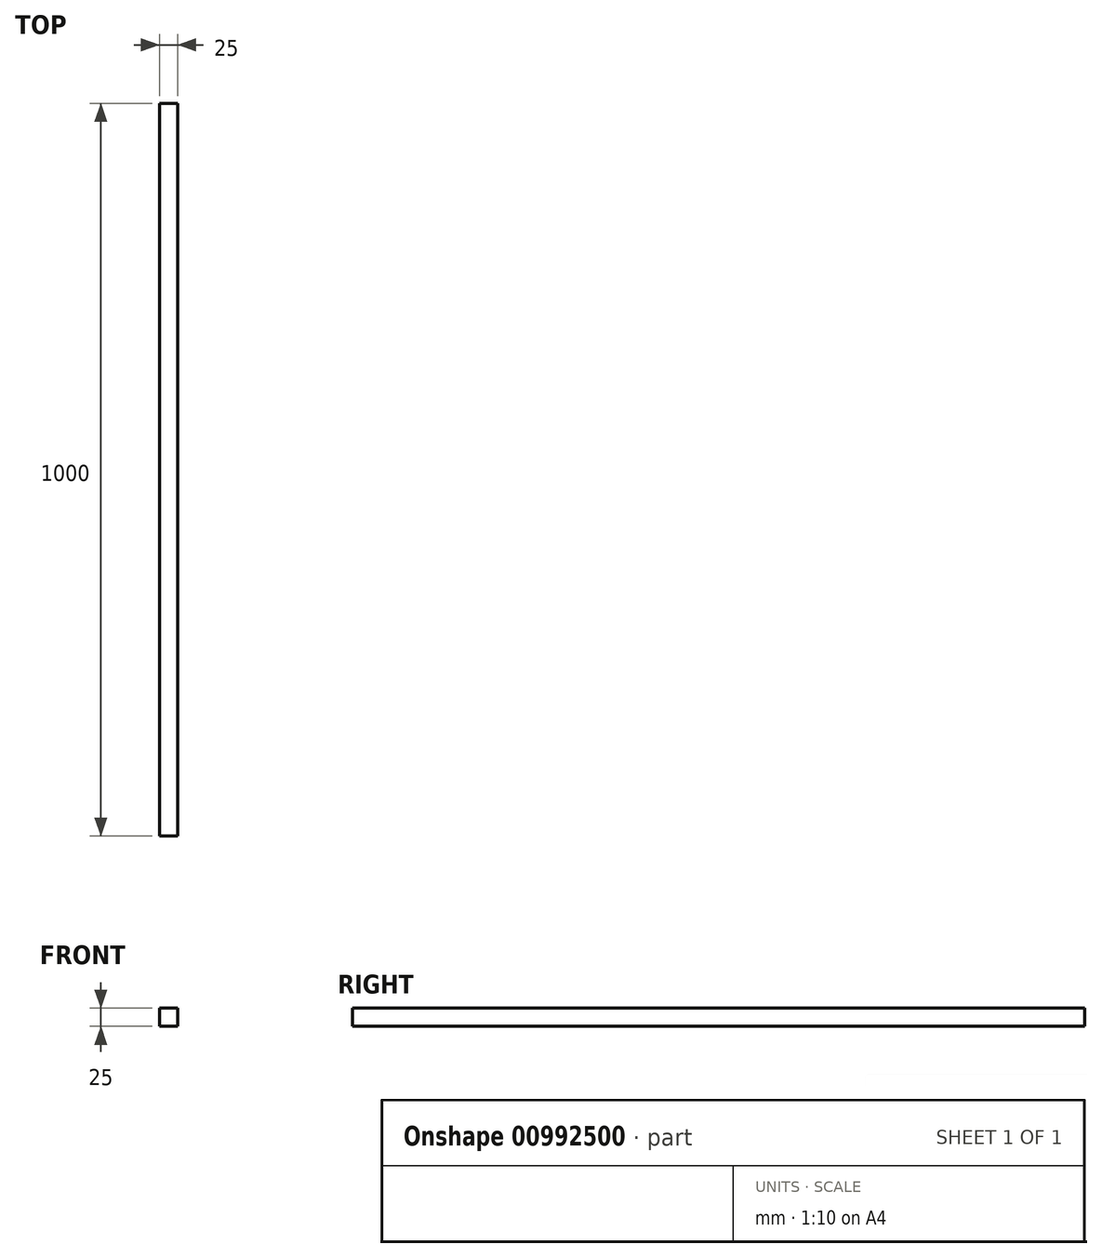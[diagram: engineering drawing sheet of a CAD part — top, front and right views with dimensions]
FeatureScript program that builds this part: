
annotation { "Feature Type Name" : "Feature", "Feature Type Description" : "" }
export const myFeature = defineFeature(function(context is Context, id is Id, definition is map)
    precondition{}
    {
        {
            var Q0;
            Q0=qCreatedBy(makeId("Top.planeOp"),FACE);
            var sketch = newSketch(context, id + "F0", { "sketchPlane" : qUnion([Q0])});
            skLineSegment(sketch, "E0.bottom", {"start": v(-93.7, 473.56) * mm, "end": v(-68.7, 473.56) * mm});
            skLineSegment(sketch, "E0.top", {"start": v(-93.7, -526.44) * mm, "end": v(-68.7, -526.44) * mm});
            skLineSegment(sketch, "E0.left", {"start": v(-93.7, 473.56) * mm, "end": v(-93.7, -526.44) * mm});
            skLineSegment(sketch, "E0.right", {"start": v(-68.7, 473.56) * mm, "end": v(-68.7, -526.44) * mm});
            skSolve(sketch);
        }
        {
            var Q0;
            Q0=makeQuery(id+"F0.imprint","IMPRINT",FACE,{"disambiguationData":[TD([[makeQuery(id+"F0.imprint","IMPRINT",EDGE,{"derivedFrom":sQuery(id+"F0.wireOp",EDGE,"E0.bottom")}),-1.0]])]});
            extrude(context, id + "F1", {"entities" : qUnion([Q0]), "depth" : 25 * mm, "offsetDistance" : 25.4 * mm});
        }
    });
